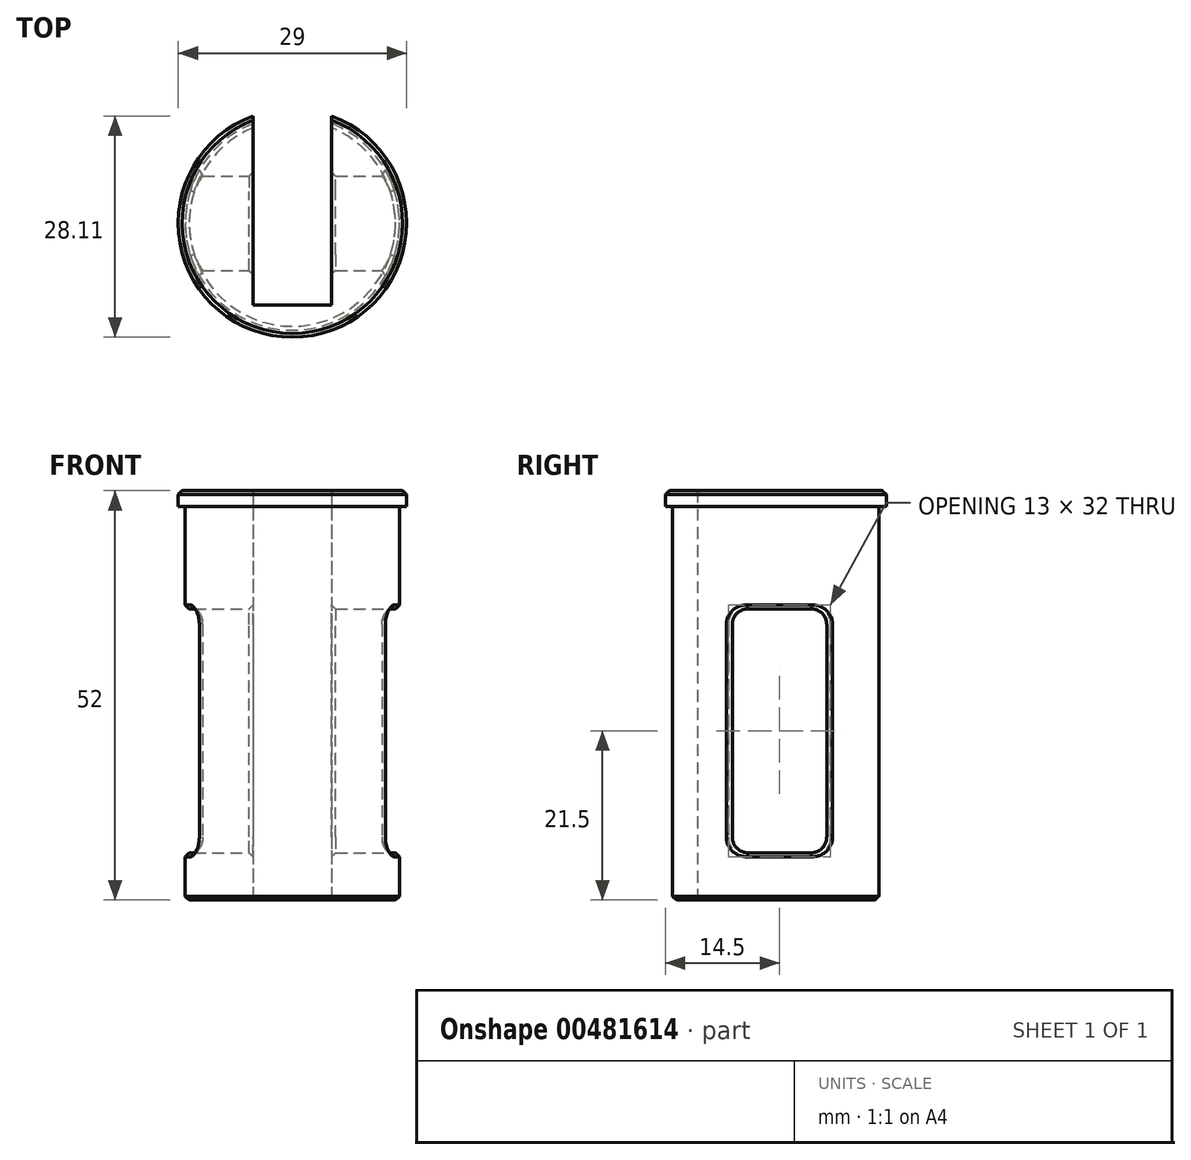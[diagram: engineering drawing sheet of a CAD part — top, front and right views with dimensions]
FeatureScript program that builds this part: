
annotation { "Feature Type Name" : "Feature", "Feature Type Description" : "" }
export const myFeature = defineFeature(function(context is Context, id is Id, definition is map)
    precondition{}
    {
        {
            var Q0;
            Q0=qCreatedBy(makeId("Top.planeOp"),FACE);
            var sketch = newSketch(context, id + "F0", { "sketchPlane" : qUnion([Q0])});
            skCircle(sketch, "E0", {"center": v(0, 0) * mm, "radius": 13.6 * mm});
            skSolve(sketch);
        }
        {
            var Q0;
            Q0 = qSketchRegion(id + "F0", true);
            extrude(context, id + "F1", {"entities" : qUnion([Q0]), "depth" : 50 * mm});
        }
        {
            var Q0;
            Q0=makeQuery(id+"F1.opExtrude","CAP_FACE",FACE,{"disambiguationData":[OSD([sQuery(id+"F0.wireOp",EDGE,"E0")])],"isStart":false});
            var sketch = newSketch(context, id + "F2", { "sketchPlane" : qUnion([Q0])});
            skCircle(sketch, "E1", {"center": v(0, 0) * mm, "radius": 14.5 * mm});
            skSolve(sketch);
        }
        {
            var Q0;
            Q0 = qSketchRegion(id + "F2", true);
            extrude(context, id + "F3", {"entities" : qUnion([Q0]), "operationType" : NewBodyOperationType.ADD, "depth" : 2 * mm});
        }
        {
            var Q0;
            Q0=makeQuery(id+"F3.opExtrude","CAP_FACE",FACE,{"disambiguationData":[OSD([sQuery(id+"F2.wireOp",EDGE,"E1")])],"isStart":false});
            chamfer(context, id + "F4", {"entities" : qUnion([Q0]), "width" : 0.5 * mm, "tangentPropagation" : true});
        }
        {
            var Q0;
            Q0=makeQuery(id+"F1.opExtrude","CAP_EDGE",EDGE,{"disambiguationData":[OSD([sQuery(id+"F0.wireOp",EDGE,"E0")])],"isStart":true});
            chamfer(context, id + "F5", {"entities" : qUnion([Q0]), "width" : 0.5 * mm, "tangentPropagation" : true});
        }
        {
            var Q0;
            Q0=makeQuery(id+"F1.opExtrude","CAP_FACE",FACE,{"disambiguationData":[OSD([sQuery(id+"F0.wireOp",EDGE,"E0")])],"isStart":true});
            var sketch = newSketch(context, id + "F6", { "sketchPlane" : qUnion([Q0])});
            skLineSegment(sketch, "E2.bottom", {"start": v(5, 10.4) * mm, "end": v(-5, 10.4) * mm});
            skLineSegment(sketch, "E2.top", {"start": v(5, -67.86) * mm, "end": v(-5, -67.86) * mm});
            skLineSegment(sketch, "E2.left", {"start": v(5, -67.86) * mm, "end": v(5, 10.4) * mm});
            skLineSegment(sketch, "E2.right", {"start": v(-5, -67.86) * mm, "end": v(-5, 10.4) * mm});
            skSolve(sketch);
        }
        {
            var Q0;
            Q0 = qSketchRegion(id + "F6", true);
            extrude(context, id + "F7", {"entities" : qUnion([Q0]), "operationType" : NewBodyOperationType.REMOVE, "endBound" : BoundingType.THROUGH_ALL, "oppositeDirection" : true, "depth" : 25.4 * mm});
        }
        {
            var Q0;
            Q0=qCreatedBy(makeId("Right.planeOp"),FACE);
            var sketch = newSketch(context, id + "F8", { "sketchPlane" : qUnion([Q0])});
            skLineSegment(sketch, "E3.bottom", {"start": v(-4, 37) * mm, "end": v(4, 37) * mm});
            skLineSegment(sketch, "E3.top", {"start": v(-4, 6) * mm, "end": v(4, 6) * mm});
            skLineSegment(sketch, "E3.left", {"start": v(-6, 35) * mm, "end": v(-6, 8) * mm});
            skLineSegment(sketch, "E3.right", {"start": v(6, 35) * mm, "end": v(6, 8) * mm});
            skPoint(sketch, "E4.visualSharp", {"position": v(-6, 37) * mm});
            skArc(sketch, "E4.filletArc", {"start": v(-4, 37) * mm, "mid": v(-5.41, 36.41) * mm, "end": v(-6, 35) * mm});
            skPoint(sketch, "E5.visualSharp", {"position": v(6, 37) * mm});
            skArc(sketch, "E5.filletArc", {"start": v(6, 35) * mm, "mid": v(5.41, 36.41) * mm, "end": v(4, 37) * mm});
            skPoint(sketch, "E6.visualSharp", {"position": v(-6, 6) * mm});
            skArc(sketch, "E6.filletArc", {"start": v(-6, 8) * mm, "mid": v(-5.41, 6.59) * mm, "end": v(-4, 6) * mm});
            skPoint(sketch, "E7.visualSharp", {"position": v(6, 6) * mm});
            skArc(sketch, "E7.filletArc", {"start": v(4, 6) * mm, "mid": v(5.41, 6.59) * mm, "end": v(6, 8) * mm});
            skSolve(sketch);
        }
        {
            var Q0;
            Q0 = qSketchRegion(id + "F8", true);
            extrude(context, id + "F9", {"entities" : qUnion([Q0]), "operationType" : NewBodyOperationType.REMOVE, "endBound" : BoundingType.SYMMETRIC, "oppositeDirection" : true, "depth" : 50.8 * mm});
        }
        {
            var Q0;
            Q0=makeQuery(id+"F9.boolean.opBoolean","INTERSECT",EDGE,{"derivedFrom":[makeQuery(id+"F7.boolean.opBoolean","COPY",FACE,{"derivedFrom":makeQuery(id+"F7.opExtrude","SWEPT_FACE",FACE,{"disambiguationData":[OSD([sQuery(id+"F6.wireOp",EDGE,"E2.left")])]})}),makeQuery(id+"F9.opExtrude","SWEPT_FACE",FACE,{"disambiguationData":[OSD([sQuery(id+"F8.wireOp",EDGE,"E6.filletArc")])]})]});
            var Q1;
            Q1=makeQuery(id+"F9.boolean.opBoolean","INTERSECT",EDGE,{"disambiguationData":[OD(0.0)],"derivedFrom":[makeQuery(id+"F1.opExtrude","SWEPT_FACE",FACE,{"disambiguationData":[OSD([sQuery(id+"F0.wireOp",EDGE,"E0")])]}),makeQuery(id+"F9.opExtrude","SWEPT_FACE",FACE,{"disambiguationData":[OSD([sQuery(id+"F8.wireOp",EDGE,"E3.left")])]})]});
            var Q2;
            Q2=makeQuery(id+"F9.boolean.opBoolean","INTERSECT",EDGE,{"disambiguationData":[OD(1.0)],"derivedFrom":[makeQuery(id+"F1.opExtrude","SWEPT_FACE",FACE,{"disambiguationData":[OSD([sQuery(id+"F0.wireOp",EDGE,"E0")])]}),makeQuery(id+"F9.opExtrude","SWEPT_FACE",FACE,{"disambiguationData":[OSD([sQuery(id+"F8.wireOp",EDGE,"E3.left")])]})]});
            var Q3;
            Q3=makeQuery(id+"F9.boolean.opBoolean","INTERSECT",EDGE,{"derivedFrom":[makeQuery(id+"F7.boolean.opBoolean","COPY",FACE,{"derivedFrom":makeQuery(id+"F7.opExtrude","SWEPT_FACE",FACE,{"disambiguationData":[OSD([sQuery(id+"F6.wireOp",EDGE,"E2.right")])]})}),makeQuery(id+"F9.opExtrude","SWEPT_FACE",FACE,{"disambiguationData":[OSD([sQuery(id+"F8.wireOp",EDGE,"E3.left")])]})]});
            chamfer(context, id + "F10", {"entities" : qUnion([Q0, Q1, Q2, Q3]), "width" : 0.5 * mm, "tangentPropagation" : true});
        }
    });
